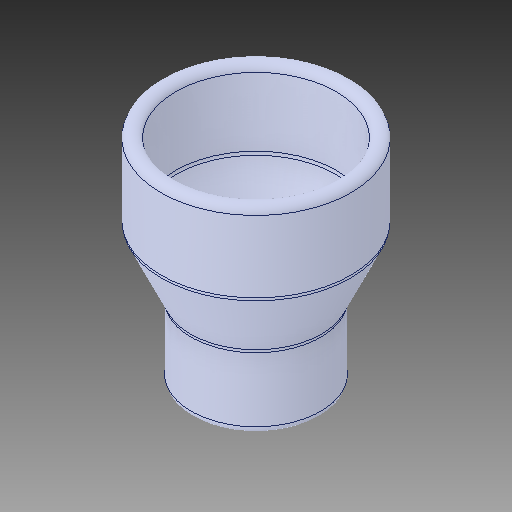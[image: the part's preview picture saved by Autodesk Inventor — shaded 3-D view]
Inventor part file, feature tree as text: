
AUTODESK INVENTOR PART (.ipt)
format: ipt  version: 2018 (Build 220112000, 112)  size: 166,912 bytes
history: native  units: in
note: dims shown in document units (in); Inventor stores cm internally (conversion verified against a paired STEP export)
features: fillet x1
ambient origin geometry x8: Origin, YZ Plane, XZ Plane, XY Plane, X Axis, Y Axis, Z Axis, Center Point
bodies: Solid1 (feature_tree)
feature tree (1):
  fillet  "Fillet4"  [1 undecoded]
note: 1 required parameter value undecoded (feature->parameter linkage not recoverable at this tier; creation-order binding heuristic only, values carry confidence <= 0.55)
